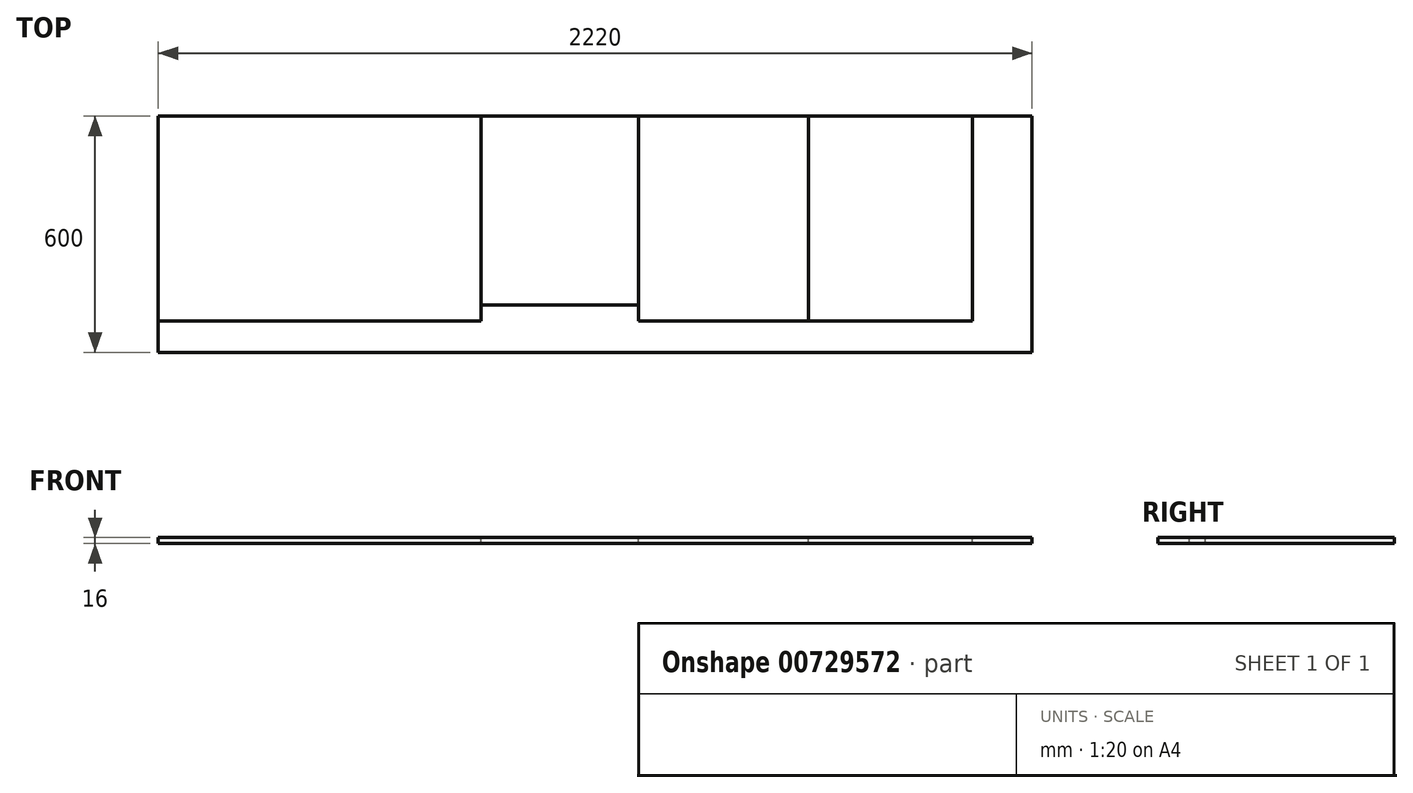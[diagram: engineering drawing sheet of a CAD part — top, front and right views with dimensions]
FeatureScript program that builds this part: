
annotation { "Feature Type Name" : "Feature", "Feature Type Description" : "" }
export const myFeature = defineFeature(function(context is Context, id is Id, definition is map)
    precondition{}
    {
        {
            var Q0;
            Q0=qCreatedBy(makeId("Top.planeOp"),FACE);
            var sketch = newSketch(context, id + "F0", { "sketchPlane" : qUnion([Q0])});
            skLineSegment(sketch, "E0.bottom", {"start": v(1110, -300) * mm, "end": v(-1110, -300) * mm});
            skLineSegment(sketch, "E0.top", {"start": v(1110, 300) * mm, "end": v(-1110, 300) * mm});
            skLineSegment(sketch, "E0.left", {"start": v(1110, -300) * mm, "end": v(1110, 300) * mm});
            skLineSegment(sketch, "E0.right", {"start": v(-1110, -300) * mm, "end": v(-1110, 300) * mm});
            skPoint(sketch, "E0.middle", {"position": v(0, 0) * mm});
            skSolve(sketch);
        }
        {
            var Q0;
            Q0=makeQuery(id+"F0.imprint","IMPRINT",FACE,{"disambiguationData":[TD([[makeQuery(id+"F0.imprint","IMPRINT",EDGE,{"derivedFrom":sQuery(id+"F0.wireOp",EDGE,"E0.bottom")}),-1.0]])]});
            extrude(context, id + "F1", {"entities" : qUnion([Q0]), "depth" : 16 * mm, "offsetDistance" : 25 * mm});
        }
        {
            var Q0;
            Q0=makeQuery(id+"F1.opExtrude","CAP_FACE",FACE,{"disambiguationData":[OSD([sQuery(id+"F0.wireOp",EDGE,"E0.bottom"),sQuery(id+"F0.wireOp",EDGE,"E0.top"),sQuery(id+"F0.wireOp",EDGE,"E0.left"),sQuery(id+"F0.wireOp",EDGE,"E0.right")])],"isStart":false});
            var sketch = newSketch(context, id + "F2", { "sketchPlane" : qUnion([Q0])});
            skLineSegment(sketch, "E1.bottom", {"start": v(-1110, 300) * mm, "end": v(-290, 300) * mm});
            skLineSegment(sketch, "E1.top", {"start": v(-1110, -220) * mm, "end": v(-290, -220) * mm});
            skLineSegment(sketch, "E1.left", {"start": v(-1110, 300) * mm, "end": v(-1110, -220) * mm});
            skLineSegment(sketch, "E1.right", {"start": v(-290, 300) * mm, "end": v(-290, -220) * mm});
            skLineSegment(sketch, "E2.left", {"start": v(-290, 300) * mm, "end": v(-290, -100) * mm});
            skLineSegment(sketch, "E3.bottom", {"start": v(-290, 300) * mm, "end": v(110, 300) * mm});
            skLineSegment(sketch, "E3.top", {"start": v(-290, -180) * mm, "end": v(110, -180) * mm});
            skLineSegment(sketch, "E3.left", {"start": v(-290, 300) * mm, "end": v(-290, -180) * mm});
            skLineSegment(sketch, "E3.right", {"start": v(110, 300) * mm, "end": v(110, -180) * mm});
            skLineSegment(sketch, "E4.bottom", {"start": v(110, 300) * mm, "end": v(542, 300) * mm});
            skLineSegment(sketch, "E4.top", {"start": v(110, -220) * mm, "end": v(542, -220) * mm});
            skLineSegment(sketch, "E4.left", {"start": v(110, 300) * mm, "end": v(110, -220) * mm});
            skLineSegment(sketch, "E4.right", {"start": v(542, 300) * mm, "end": v(542, -220) * mm});
            skLineSegment(sketch, "E5.bottom", {"start": v(542, 300) * mm, "end": v(958, 300) * mm});
            skLineSegment(sketch, "E5.top", {"start": v(542, -220) * mm, "end": v(958, -220) * mm});
            skLineSegment(sketch, "E5.right", {"start": v(958, 300) * mm, "end": v(958, -220) * mm});
            skSolve(sketch);
        }
        {
            var Q0;
            {var subQ1=sQuery(id+"F2.wireOp",EDGE,"E1.bottom");Q0=makeQuery(id+"F2.imprint","IMPRINT",FACE,{"disambiguationData":[TD([[makeQuery(id+"F2.imprint","IMPRINT",EDGE,{"derivedFrom":subQ1}),1.0]])]});}
            extrude(context, id + "F3", {"entities" : qUnion([Q0]), "oppositeDirection" : true, "depth" : 16 * mm, "offsetDistance" : 25 * mm});
        }
        {
            var Q0;
            {var subQ3=sQuery(id+"F2.wireOp",EDGE,"E3.bottom");Q0=makeQuery(id+"F2.imprint","IMPRINT",FACE,{"disambiguationData":[TD([[makeQuery(id+"F2.imprint","IMPRINT",EDGE,{"derivedFrom":subQ3}),1.0]])]});}
            extrude(context, id + "F4", {"entities" : qUnion([Q0]), "oppositeDirection" : true, "depth" : 16 * mm, "offsetDistance" : 25 * mm});
        }
        {
            var Q0;
            {var subQ3=sQuery(id+"F2.wireOp",EDGE,"E4.bottom");Q0=makeQuery(id+"F2.imprint","IMPRINT",FACE,{"disambiguationData":[TD([[makeQuery(id+"F2.imprint","IMPRINT",EDGE,{"derivedFrom":subQ3}),1.0]])]});}
            extrude(context, id + "F5", {"entities" : qUnion([Q0]), "oppositeDirection" : true, "depth" : 16 * mm, "offsetDistance" : 25 * mm});
        }
        {
            var Q0;
            Q0=makeQuery(id+"F2.imprint","IMPRINT",FACE,{"disambiguationData":[TD([[makeQuery(id+"F2.imprint","IMPRINT",EDGE,{"derivedFrom":sQuery(id+"F2.wireOp",EDGE,"E5.bottom")}),1.0]])]});
            extrude(context, id + "F6", {"entities" : qUnion([Q0]), "oppositeDirection" : true, "depth" : 16 * mm, "offsetDistance" : 25 * mm});
        }
    });
